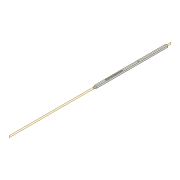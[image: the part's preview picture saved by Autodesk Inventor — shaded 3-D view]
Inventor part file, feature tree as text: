
AUTODESK INVENTOR PART (.ipt)
format: ipt  version: 2022 (Build 260153000, 153)  size: 124,416 bytes
history: native  units: mm
features: extrude x2, sketch x2, projected_geometry x1
ambient origin geometry x8: Origin, YZ Plane, XZ Plane, XY Plane, X Axis, Y Axis, Z Axis, Center Point
bodies: Solid1 (feature_tree)
feature tree (5):
  extrude  "Extrusion1"  Depth=405.743mm
  extrude  "Extrusion2"  Depth=3.0mm
  sketch  "Sketch1"  dims[d0=8.0mm d1=405.743mm]
  sketch  "Sketch2"  dims[d2=3.0mm d3=3.0mm d4=6.0mm d5=0.0mm d20=3.0mm d21=58.68mm d22=117.0mm d23=8.0mm d24=100.0mm d25=4.363323mm d26=4.363323mm d27=10.0mm d28=0.0mm]
  projected_geometry  "Projected Loop1"
